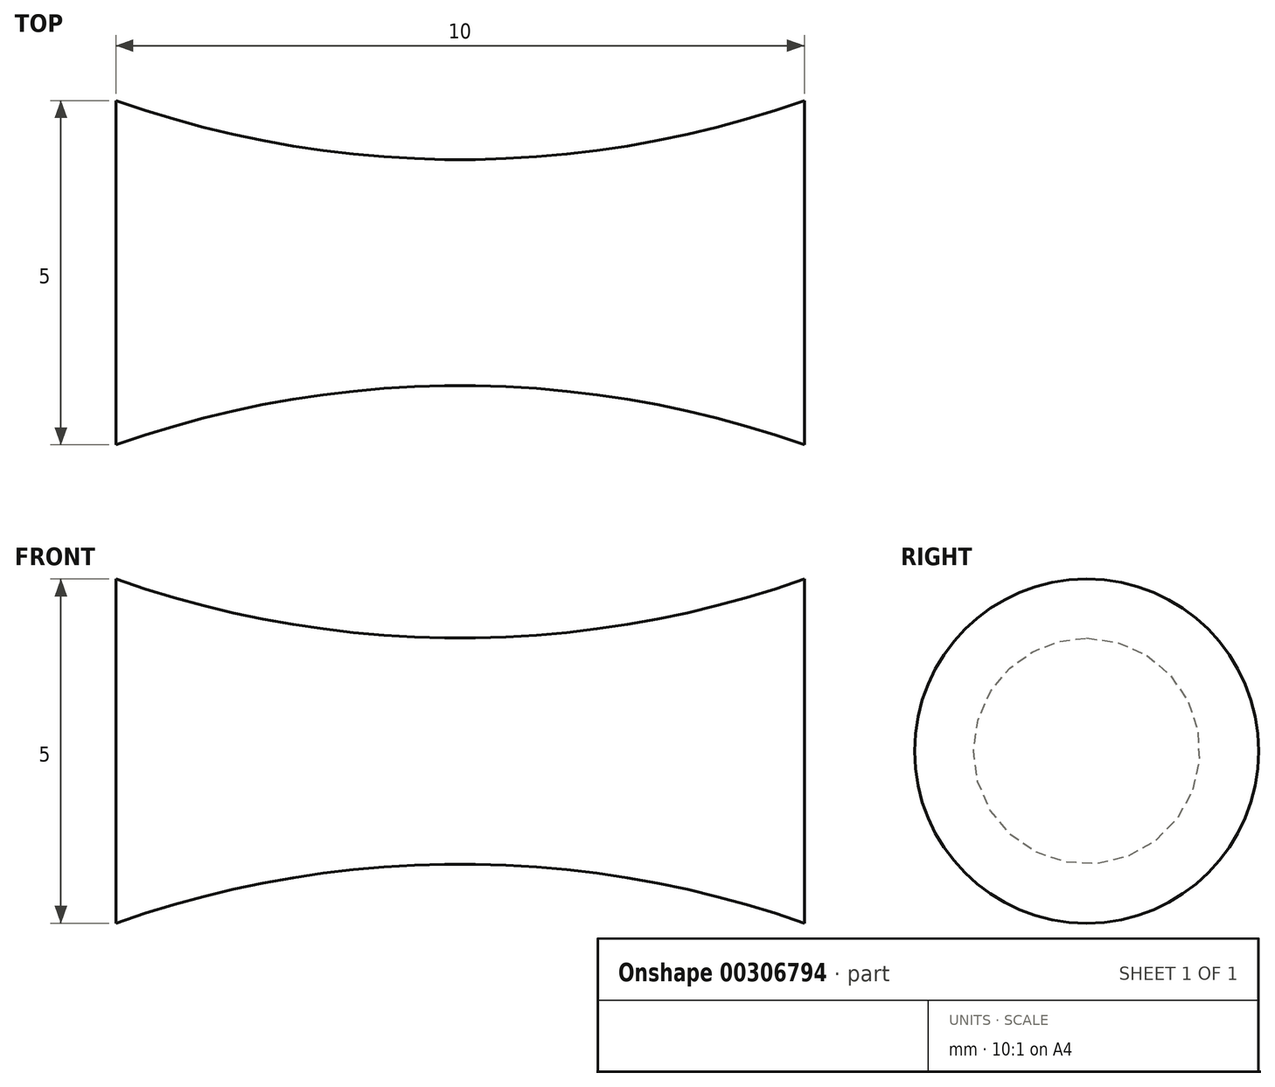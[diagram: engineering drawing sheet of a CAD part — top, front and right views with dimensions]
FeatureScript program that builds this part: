
annotation { "Feature Type Name" : "Feature", "Feature Type Description" : "" }
export const myFeature = defineFeature(function(context is Context, id is Id, definition is map)
    precondition{}
    {
        {
            var Q0;
            Q0=qCreatedBy(makeId("Front.planeOp"),FACE);
            var sketch = newSketch(context, id + "F0", { "sketchPlane" : qUnion([Q0])});
            skLineSegment(sketch, "E0.left", {"start": v(-5, 2.5) * mm, "end": v(-5, 0) * mm});
            skLineSegment(sketch, "E0.right", {"start": v(5, 2.5) * mm, "end": v(5, 0) * mm});
            skPoint(sketch, "E0.middle", {"position": v(0, 0) * mm});
            skArc(sketch, "E1", {"start": v(-5, 2.5) * mm, "mid": v(0, 1.64) * mm, "end": v(5, 2.5) * mm});
            skLineSegment(sketch, "E2", {"start": v(-5, 0) * mm, "end": v(5, 0) * mm});
            skSolve(sketch);
        }
        {
            var Q0;
            Q0=makeQuery(id+"F0.imprint","IMPRINT",FACE,{"disambiguationData":[TD([[makeQuery(id+"F0.imprint","IMPRINT",EDGE,{"derivedFrom":sQuery(id+"F0.wireOp",EDGE,"E0.left")}),1.0]])]});
            var Q1;
            Q1=sQuery(id+"F0.wireOp",EDGE,"E2");
            revolve(context, id + "F1", {"entities" : qUnion([Q0]), "axis" : qUnion([Q1]), "revolveType" : RevolveType.FULL});
        }
    });
